# Revit family: AP-5102
name_source: partatom
category: Communication Devices
revit_build: Autodesk Revit Architecture 2012 (Build: 20110309_2315(x64)
units: mm (PartAtom-declared; Revit-internal decimal feet)

## types (1)
- AP-5102
    Coverage Horizontal = 105.00°
    Coverage Vertical = 105.00°
    Default Elevation = 0 mm
    Depth = 267 mm
    Description = 10-inch, Two-way Trapezoidal Enclosure with 105-degree Axisymmetric Coverage
10-inch, Two-way Trapezoidal Enclosure with 105-degree Axisymmetric Coverage
    Grill Apex to Apex = 231 mm
    Grill Height = 525 mm
    Grill Rear Offset from Front = 37 mm
    Height = 559 mm
    Impedance = 8
    Manufacturer = QSC Audio Products, LLC
    Manufacturer URL = www.qscaudio.com
    Model = AP-5102
    Power Handling = 450
    Product Documentation Link = http://qscmarketing.com
    Product Page URL = http://www.qsc.com
    Rear Face Width = 164 mm
    Regulatory Compliance = RoHS
    SPL Max = 127
    Sensitivity = 94
    Taper Offset from Front = 56 mm
    URL = http://www.qsc.com
    Weight Dimensional (kg) = 24
    Weight Dimensional (lb) = 53
    Weight Product (kg) = 21.7
    Weight Product (lb) = 48
    Width = 305 mm

## geometry (parser evidence)
native form markers: Blend x2, Sweep x1
no freeform markers — native parametric forms only
